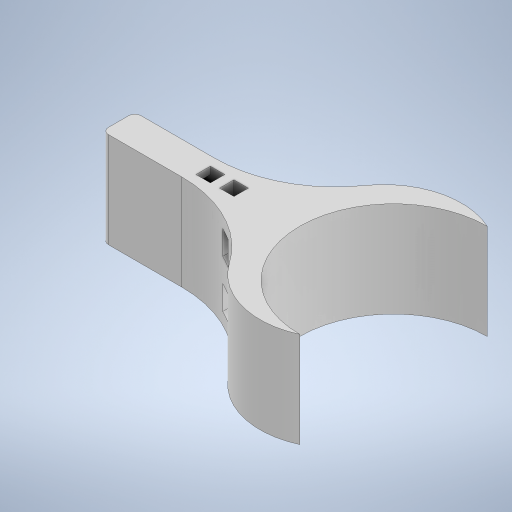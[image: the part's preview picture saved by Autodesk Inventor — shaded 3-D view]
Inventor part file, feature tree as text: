
AUTODESK INVENTOR PART (.ipt)
format: ipt  version: 2023 (Build 270158000, 158)  size: 328,192 bytes
history: native  units: in
note: dims shown in document units (in); Inventor stores cm internally (conversion verified against a paired STEP export)
features: projected_geometry x5, extrude x4, sketch x4, fillet x1
ambient origin geometry x8: Origin, YZ Plane, XZ Plane, XY Plane, X Axis, Y Axis, Z Axis, Center Point
bodies: Solid1 (feature_tree)
feature tree (14):
  extrude  "Extrusion1"  Depth=0.27in
  extrude  "Extrusion2"  Depth=0.79in
  extrude  "Extrusion3"  Depth=0.27in
  extrude  "Extrusion4"  Depth=1.0in
  fillet  "Fillet1"  Radius=1.0in
  sketch  "Sketch1"  dims[d0=1.15in d1=0.27in]
  sketch  "Sketch3"  dims[d2=0.79in d3=0.0in d4=0.15in]
  projected_geometry  "Projected Loop1"
  projected_geometry  "Projected Loop2"
  projected_geometry  "Projected Loop3"
  sketch  "Sketch4"  dims[d5=1.55in d6=0.27in]
  sketch  "Sketch5"  dims[d7=0.2in d8=1.0in d9=1.0in d10=180.0deg d11=90.0deg d12=90.0deg d13=1.15in d14=0.1in d15=0.2in d16=0.0975in d17=0.0975in d18=0.0in d19=0.0in d25=0.11in d26=0.67in d27=0.06in d28=0.06in d29=0.7in d30=0.12in d31=0.12in d32=0.075in d33=0.12in d34=0.12in d35=0.195in d36=0.0in d37=0.075in d38=0.0in d39=0.05in]
  projected_geometry  "Projected Loop4"
  projected_geometry  "Projected Loop5"
